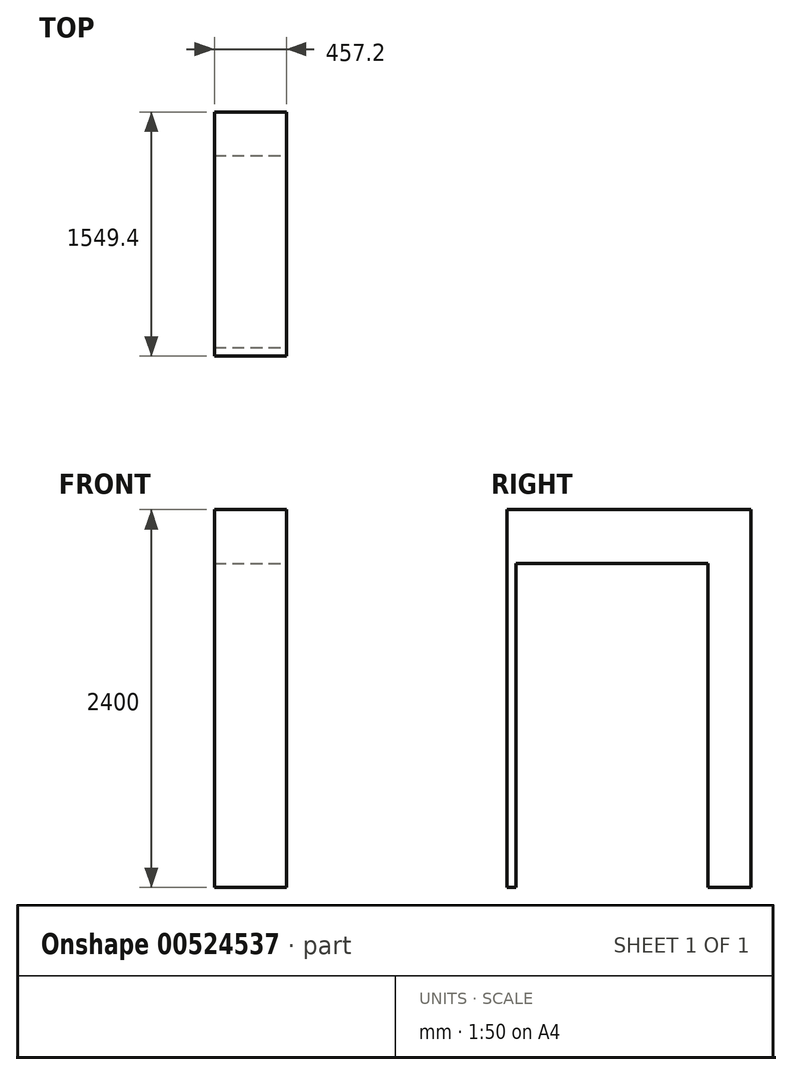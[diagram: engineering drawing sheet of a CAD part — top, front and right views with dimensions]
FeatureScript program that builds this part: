
annotation { "Feature Type Name" : "Feature", "Feature Type Description" : "" }
export const myFeature = defineFeature(function(context is Context, id is Id, definition is map)
    precondition{}
    {
        {
            var Q0;
            Q0=qCreatedBy(makeId("Top.planeOp"),FACE);
            var sketch = newSketch(context, id + "F0", { "sketchPlane" : qUnion([Q0])});
            skLineSegment(sketch, "E0.bottom", {"start": v(0, 0) * mm, "end": v(457.2, 0) * mm});
            skLineSegment(sketch, "E0.top", {"start": v(0, 1549.4) * mm, "end": v(457.2, 1549.4) * mm});
            skLineSegment(sketch, "E0.left", {"start": v(0, 0) * mm, "end": v(0, 1549.4) * mm});
            skLineSegment(sketch, "E0.right", {"start": v(457.2, 0) * mm, "end": v(457.2, 1549.4) * mm});
            skSolve(sketch);
        }
        {
            var Q0;
            Q0 = qSketchRegion(id + "F0", true);
            extrude(context, id + "F1", {"entities" : qUnion([Q0]), "depth" : 2400 * mm, "offsetDistance" : 25 * mm});
        }
        {
            var Q0;
            Q0=makeQuery(id+"F1.opExtrude","SWEPT_FACE",FACE,{"disambiguationData":[OSD([sQuery(id+"F0.wireOp",EDGE,"E0.right")])]});
            var sketch = newSketch(context, id + "F2", { "sketchPlane" : qUnion([Q0])});
            skLineSegment(sketch, "E1.bottom", {"start": v(55, 0) * mm, "end": v(1275, 0) * mm});
            skLineSegment(sketch, "E1.top", {"start": v(55, 2057.4) * mm, "end": v(1275, 2057.4) * mm});
            skLineSegment(sketch, "E1.left", {"start": v(55, 0) * mm, "end": v(55, 2057.4) * mm});
            skLineSegment(sketch, "E1.right", {"start": v(1275, 0) * mm, "end": v(1275, 2057.4) * mm});
            skSolve(sketch);
        }
        {
            var Q0;
            Q0 = qSketchRegion(id + "F2", true);
            extrude(context, id + "F3", {"entities" : qUnion([Q0]), "operationType" : NewBodyOperationType.REMOVE, "endBound" : BoundingType.UP_TO_NEXT, "oppositeDirection" : true, "depth" : 25 * mm, "offsetDistance" : 25 * mm});
        }
    });
